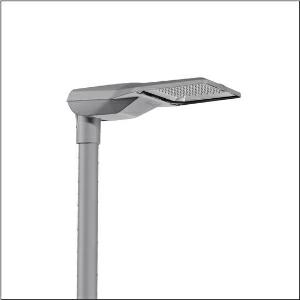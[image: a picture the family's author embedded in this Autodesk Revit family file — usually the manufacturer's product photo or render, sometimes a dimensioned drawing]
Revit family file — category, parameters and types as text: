
# Revit family: streetlight_sl_21_midi___stw1_0a_5xe7e43a08nb_d775
name_source: partatom
category: Lighting Fixtures
units: mm (PartAtom-declared; Revit-internal decimal feet)

## family parameters
Cut with Voids When Loaded = No
Host = Face
Light Source = No
Part Type = Normal
Room Calculation Point = No
Round Connector Dimension = Use Diameter
Shared = No

## types (1)
- --- (1 x LED, 23710 lm, 151.2 W, 4000K)
    Apparent Load = 151 VA
    CIE Flux Codes = 39 75 98 100 100
    Color Rendering = 70
    Color Temperature = 4000K
    Default Elevation = 1800 mm
    Description = Streetlight SL 21 midi, mast luminaire, primary light control with lens, of PMMA, primary optical cover: cover, of toughened safety glass, transparent, light distribution: STW1.0a, light emission: direct distribution, primary light characteristic: asymmetric, installation type: post-top, side-entry, LED, 3G 1.5mm², High Power LED, rated luminous flux: 23.710lm, luminous efficacy: 157lm/W, light colour: 740, colour temperature: 4000K, control: overheat protection, constant luminous flux control, time-dependent luminous flux control, flexible luminous flux parameterisation, mains connection: 220..240V, AC, 50/60Hz, connection cable pre-assembled, cable length: 12,5m, wiring characteristics: H07RN-F, start of lifetime: 151W, end of service life: 157W, reduction: 71W, luminaire housing, of diecast aluminium, powder-coated, Siteco® metallic grey (DB 702S), corrosivity category C5 mid according to DIN EN ISO 12944, please order mast flange separately, inclination adjustable: 0°, 5°, 10°, 15°, sealing non-destructively replaceable, multi-level sealing system, length: 644mm, width: 335mm, height: 110mm, mast flange for spigot size: 42mm (side-entry): 5XC10008XM4, 60/48mm (side-entry/post-top): 5XC10108XM2, 76/60mm (side-entry/post-top): 5XC10108XM1, protection rating (complete): IP66, insulation class (complete): insulation class II (safety insulation), certification: CE, ENEC, ENEC+, VDE, impact resistance: IK09, permissible operating ambient temperature for outdoor applications: -40..+50°C, standard-compliant lighting for roads and squares, packaging unit: 1 piece

Light Distribution: STW1.0a
    Height = 111 mm
    Lamp = 1 x LED
    Lamp Light Flux = 23710 lm
    Lamp Power = 151.2 W
    Lamp count = 1
    Length = 644 mm
    Luminous efficacy = 157 lm/W
    Manufacturer = Siteco
    ModVariant = No
    Model = 5XE7E43A08NB
    Number of Poles = 1
    OnlyDefault = Yes
    Power Factor = 1
    Product Name = Streetlight SL 21 midi | STW1.0a
    Product group = mast luminaire | pylon top
    ProductGroupID = 6100
    Protection Class = Protection class II
    Protection Degree = IP 66
    RLX_Detail_Level = 1
    RLX_Emergency_Light_Flux = 0 lm
    RLX_Emergency_Type = 0
    RLX_Emergency_Type_DB = No
    RlxData = <blob elided: 90661 chars, md5=da77cced>
    Socket = socket
    Standby Power = 0 W
    System Light Flux = 23710 lm
    System Power = 151 W
    Type Comments = factory setting: luminous flux: 100 % | Output Level: 100 % | 802 mA
    Type Image = l_1004298.jpg
    URL = http://relux.com
    VarID = @adj_119815
    Voltage = 0 V
    Weight = 0.00 kg
    Width = 336 mm

## geometry (parser evidence)
native form markers: Blend x4, Sweep x12
no freeform markers — native parametric forms only
